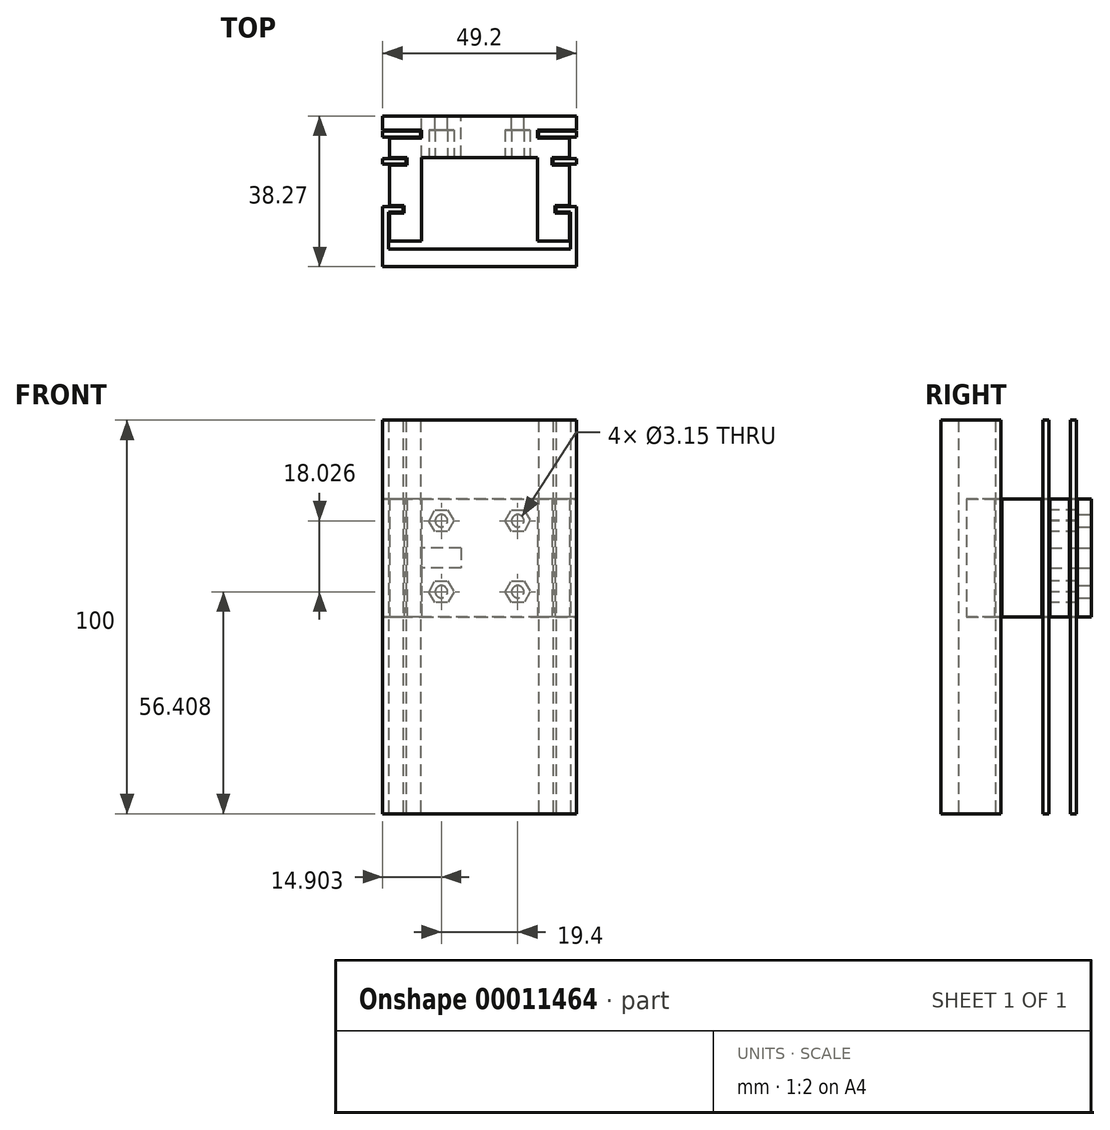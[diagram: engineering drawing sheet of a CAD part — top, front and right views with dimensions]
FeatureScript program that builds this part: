
annotation { "Feature Type Name" : "Feature", "Feature Type Description" : "" }
export const myFeature = defineFeature(function(context is Context, id is Id, definition is map)
    precondition{}
    {
        {
            var Q0;
            Q0=qCreatedBy(makeId("Top.planeOp"),FACE);
            var sketch = newSketch(context, id + "F0", { "sketchPlane" : qUnion([Q0])});
            skLineSegment(sketch, "E0.rect.bottom", {"start": v(-23.27, 11.03) * mm, "end": v(25.93, 11.03) * mm});
            skLineSegment(sketch, "E0.rect.top", {"start": v(-23.27, -23.37) * mm, "end": v(25.93, -23.37) * mm});
            skLineSegment(sketch, "E0.rect.left", {"start": v(-23.27, 11.03) * mm, "end": v(-23.27, -23.37) * mm});
            skLineSegment(sketch, "E0.rect.right", {"start": v(25.93, 11.03) * mm, "end": v(25.93, -23.37) * mm});
            skPoint(sketch, "E0.rect.middle", {"position": v(1.33, -6.17) * mm});
            skLineSegment(sketch, "E1", {"start": v(-13.62, 11.03) * mm, "end": v(-13.62, 9.53) * mm});
            skLineSegment(sketch, "E2", {"start": v(-13.62, 9.53) * mm, "end": v(-23.27, 9.53) * mm});
            skLineSegment(sketch, "E3", {"start": v(-23.27, 9.53) * mm, "end": v(-23.27, 4.13) * mm});
            skLineSegment(sketch, "E4", {"start": v(-23.27, 4.13) * mm, "end": v(-17.37, 4.13) * mm});
            skLineSegment(sketch, "E5", {"start": v(-17.37, 4.13) * mm, "end": v(-17.37, 2.63) * mm});
            skLineSegment(sketch, "E6", {"start": v(-17.37, 2.63) * mm, "end": v(-23.27, 2.63) * mm});
            skLineSegment(sketch, "E7", {"start": v(-23.27, 2.63) * mm, "end": v(-23.27, -8.04) * mm});
            skLineSegment(sketch, "E8", {"start": v(-23.27, -8.04) * mm, "end": v(-18.07, -8.04) * mm});
            skLineSegment(sketch, "E9", {"start": v(-18.07, -8.04) * mm, "end": v(-18.07, -9.54) * mm});
            skLineSegment(sketch, "E10", {"start": v(-18.07, -9.54) * mm, "end": v(-23.27, -9.54) * mm});
            skLineSegment(sketch, "E11", {"start": v(16.28, 11.03) * mm, "end": v(16.28, 9.53) * mm});
            skLineSegment(sketch, "E12", {"start": v(16.28, 9.53) * mm, "end": v(25.93, 9.53) * mm});
            skLineSegment(sketch, "E13", {"start": v(25.93, 9.53) * mm, "end": v(25.93, 4.13) * mm});
            skLineSegment(sketch, "E14", {"start": v(25.93, 4.13) * mm, "end": v(20.03, 4.13) * mm});
            skLineSegment(sketch, "E15", {"start": v(20.03, 4.13) * mm, "end": v(20.03, 2.63) * mm});
            skLineSegment(sketch, "E16", {"start": v(20.03, 2.63) * mm, "end": v(25.93, 2.63) * mm});
            skLineSegment(sketch, "E17", {"start": v(25.93, 2.63) * mm, "end": v(25.93, -6.17) * mm});
            skLineSegment(sketch, "E18", {"start": v(25.93, -8.04) * mm, "end": v(20.73, -8.04) * mm});
            skLineSegment(sketch, "E19", {"start": v(20.73, -8.04) * mm, "end": v(20.73, -9.54) * mm});
            skLineSegment(sketch, "E20", {"start": v(20.73, -9.54) * mm, "end": v(25.93, -9.54) * mm});
            skLineSegment(sketch, "E21", {"start": v(-21.77, 11.03) * mm, "end": v(-21.77, -18.87) * mm});
            skLineSegment(sketch, "E22", {"start": v(-21.77, -18.87) * mm, "end": v(24.43, -18.87) * mm});
            skLineSegment(sketch, "E23", {"start": v(24.43, -18.87) * mm, "end": v(24.43, 9.53) * mm});
            skLineSegment(sketch, "E24", {"start": v(-21.77, 11.28) * mm, "end": v(-21.77, 15.19) * mm});
            skLineSegment(sketch, "E25", {"start": v(-21.77, 15.19) * mm, "end": v(24.43, 15.19) * mm});
            skLineSegment(sketch, "E26", {"start": v(24.43, 15.19) * mm, "end": v(24.43, 11.28) * mm});
            skLineSegment(sketch, "E27", {"start": v(24.43, 11.28) * mm, "end": v(16.03, 11.28) * mm});
            skLineSegment(sketch, "E28", {"start": v(16.03, 11.28) * mm, "end": v(16.03, 9.28) * mm});
            skLineSegment(sketch, "E29", {"start": v(16.03, 9.28) * mm, "end": v(24.18, 9.28) * mm});
            skLineSegment(sketch, "E30", {"start": v(24.18, 9.28) * mm, "end": v(24.18, 4.38) * mm});
            skLineSegment(sketch, "E31", {"start": v(24.18, 4.38) * mm, "end": v(19.78, 4.38) * mm});
            skLineSegment(sketch, "E32", {"start": v(19.78, 4.38) * mm, "end": v(19.78, 2.38) * mm});
            skLineSegment(sketch, "E33", {"start": v(19.78, 2.38) * mm, "end": v(24.18, 2.38) * mm});
            skLineSegment(sketch, "E34", {"start": v(24.18, 2.38) * mm, "end": v(24.18, -7.79) * mm});
            skLineSegment(sketch, "E35", {"start": v(24.18, -7.79) * mm, "end": v(20.48, -7.79) * mm});
            skLineSegment(sketch, "E36", {"start": v(20.48, -7.79) * mm, "end": v(20.48, -9.79) * mm});
            skLineSegment(sketch, "E37", {"start": v(20.48, -9.79) * mm, "end": v(24.18, -9.79) * mm});
            skLineSegment(sketch, "E38", {"start": v(24.18, -9.79) * mm, "end": v(24.18, -13.4) * mm});
            skLineSegment(sketch, "E39", {"start": v(24.18, -13.4) * mm, "end": v(-21.52, -13.4) * mm});
            skLineSegment(sketch, "E40", {"start": v(-21.52, -13.4) * mm, "end": v(-21.52, -9.79) * mm});
            skLineSegment(sketch, "E41", {"start": v(-21.52, -9.79) * mm, "end": v(-17.82, -9.79) * mm});
            skLineSegment(sketch, "E42", {"start": v(-17.82, -9.79) * mm, "end": v(-17.82, -7.79) * mm});
            skLineSegment(sketch, "E43", {"start": v(-17.82, -7.79) * mm, "end": v(-21.52, -7.79) * mm});
            skLineSegment(sketch, "E44", {"start": v(-21.52, -7.79) * mm, "end": v(-21.52, 2.38) * mm});
            skLineSegment(sketch, "E45", {"start": v(-21.52, 2.38) * mm, "end": v(-17.12, 2.38) * mm});
            skLineSegment(sketch, "E46", {"start": v(-17.12, 2.38) * mm, "end": v(-17.12, 4.38) * mm});
            skLineSegment(sketch, "E47", {"start": v(-17.12, 4.38) * mm, "end": v(-21.52, 4.38) * mm});
            skLineSegment(sketch, "E48", {"start": v(-21.52, 4.38) * mm, "end": v(-21.52, 9.28) * mm});
            skLineSegment(sketch, "E49", {"start": v(-21.52, 9.28) * mm, "end": v(-13.37, 9.28) * mm});
            skLineSegment(sketch, "E50", {"start": v(-13.37, 9.28) * mm, "end": v(-13.37, 11.28) * mm});
            skLineSegment(sketch, "E51", {"start": v(-13.37, 11.28) * mm, "end": v(-21.77, 11.28) * mm});
            skLineSegment(sketch, "E52", {"start": v(-21.52, -11.6) * mm, "end": v(-21.77, -11.6) * mm});
            skLineSegment(sketch, "E53", {"start": v(-21.52, -2.7) * mm, "end": v(-21.77, -2.7) * mm});
            skLineSegment(sketch, "E54", {"start": v(-17.82, -8.43) * mm, "end": v(-18.07, -8.43) * mm});
            skLineSegment(sketch, "E55", {"start": v(-17.12, 3.38) * mm, "end": v(-17.37, 3.38) * mm});
            skLineSegment(sketch, "E56", {"start": v(-19.67, -9.79) * mm, "end": v(-19.67, -9.54) * mm});
            skLineSegment(sketch, "E57", {"start": v(-19.3, -8.04) * mm, "end": v(-19.3, -7.79) * mm});
            skLineSegment(sketch, "E58", {"start": v(-18.52, 2.38) * mm, "end": v(-18.52, 2.63) * mm});
            skLineSegment(sketch, "E59", {"start": v(-18.54, 4.13) * mm, "end": v(-18.54, 4.38) * mm});
            skLineSegment(sketch, "E60", {"start": v(-18.03, 9.28) * mm, "end": v(-18.03, 9.53) * mm});
            skLineSegment(sketch, "E61", {"start": v(-18.25, 11.03) * mm, "end": v(-18.25, 11.28) * mm});
            skLineSegment(sketch, "E62", {"start": v(16.03, 10.24) * mm, "end": v(16.28, 10.24) * mm});
            skLineSegment(sketch, "E63", {"start": v(24.18, 7.36) * mm, "end": v(24.43, 7.36) * mm});
            skLineSegment(sketch, "E64", {"start": v(19.78, 3.38) * mm, "end": v(20.03, 3.38) * mm});
            skLineSegment(sketch, "E65", {"start": v(24.18, -1.9) * mm, "end": v(24.43, -1.9) * mm});
            skLineSegment(sketch, "E66", {"start": v(20.48, -8.79) * mm, "end": v(20.73, -8.79) * mm});
            skLineSegment(sketch, "E67", {"start": v(24.18, -11.6) * mm, "end": v(24.43, -11.6) * mm});
            skLineSegment(sketch, "E68", {"start": v(-13.62, 10.28) * mm, "end": v(-13.37, 10.28) * mm});
            skSolve(sketch);
        }
        {
            var Q0;
            {var subQ13=sQuery(id+"F0.wireOp",EDGE,"E0.rect.top");Q0=makeQuery(id+"F0.imprint","IMPRINT",FACE,{"disambiguationData":[TD([[makeQuery(id+"F0.imprint","IMPRINT",EDGE,{"derivedFrom":subQ13}),1.0]])]});}
            var Q1;
            {var subQ3=sQuery(id+"F0.wireOp",EDGE,"E8");var subQ10=makeQuery(id+"F0.imprint","INTERSECT",VERTEX,{"derivedFrom":[subQ3,sQuery(id+"F0.wireOp",EDGE,"E57")]});Q1=makeQuery(id+"F0.imprint","IMPRINT",FACE,{"disambiguationData":[TD([[makeQuery(id+"F0.imprint","IMPRINT",EDGE,{"disambiguationData":[TD([[subQ10,1.0]])],"derivedFrom":subQ3}),-1.0]])]});}
            var Q2;
            {var subQ1=sQuery(id+"F0.wireOp",EDGE,"E10");var subQ5=sQuery(id+"F0.wireOp",EDGE,"E0.rect.left");var subQ6=makeQuery(id+"F0.imprint","INTERSECT",VERTEX,{"derivedFrom":[subQ5,subQ1]});Q2=makeQuery(id+"F0.imprint","IMPRINT",FACE,{"disambiguationData":[TD([[makeQuery(id+"F0.imprint","IMPRINT",EDGE,{"disambiguationData":[TD([[subQ6,1.0]])],"derivedFrom":subQ1}),-1.0]])]});}
            var Q3;
            {var subQ7=sQuery(id+"F0.wireOp",EDGE,"E7");Q3=makeQuery(id+"F0.imprint","IMPRINT",FACE,{"disambiguationData":[TD([[makeQuery(id+"F0.imprint","IMPRINT",EDGE,{"derivedFrom":subQ7}),1.0]])]});}
            var Q4;
            {var subQ0=sQuery(id+"F0.wireOp",EDGE,"E21");var subQ3=sQuery(id+"F0.wireOp",EDGE,"E4");var subQ4=makeQuery(id+"F0.imprint","INTERSECT",VERTEX,{"derivedFrom":[subQ3,subQ0]});Q4=makeQuery(id+"F0.imprint","IMPRINT",FACE,{"disambiguationData":[TD([[makeQuery(id+"F0.imprint","IMPRINT",EDGE,{"disambiguationData":[TD([[subQ4,-1.0]])],"derivedFrom":subQ0}),-1.0]])]});}
            var Q5;
            {var subQ3=sQuery(id+"F0.wireOp",EDGE,"E4");var subQ10=makeQuery(id+"F0.imprint","INTERSECT",VERTEX,{"derivedFrom":[subQ3,sQuery(id+"F0.wireOp",EDGE,"E59")]});Q5=makeQuery(id+"F0.imprint","IMPRINT",FACE,{"disambiguationData":[TD([[makeQuery(id+"F0.imprint","IMPRINT",EDGE,{"disambiguationData":[TD([[subQ10,1.0]])],"derivedFrom":subQ3}),-1.0]])]});}
            var Q6;
            {var subQ6=sQuery(id+"F0.wireOp",EDGE,"E3");Q6=makeQuery(id+"F0.imprint","IMPRINT",FACE,{"disambiguationData":[TD([[makeQuery(id+"F0.imprint","IMPRINT",EDGE,{"derivedFrom":subQ6}),1.0]])]});}
            var Q7;
            {var subQ3=sQuery(id+"F0.wireOp",EDGE,"E0.rect.bottom");var subQ5=sQuery(id+"F0.wireOp",EDGE,"E0.rect.left");var subQ7=makeQuery(id+"F0.imprint","INTERSECT",VERTEX,{"derivedFrom":[subQ3,subQ5]});Q7=makeQuery(id+"F0.imprint","IMPRINT",FACE,{"disambiguationData":[TD([[makeQuery(id+"F0.imprint","IMPRINT",EDGE,{"disambiguationData":[TD([[subQ7,-1.0]])],"derivedFrom":subQ3}),-1.0]])]});}
            var Q8;
            {var subQ0=sQuery(id+"F0.wireOp",EDGE,"E21");var subQ3=sQuery(id+"F0.wireOp",EDGE,"E0.rect.bottom");var subQ4=makeQuery(id+"F0.imprint","INTERSECT",VERTEX,{"derivedFrom":[subQ3,subQ0]});Q8=makeQuery(id+"F0.imprint","IMPRINT",FACE,{"disambiguationData":[TD([[makeQuery(id+"F0.imprint","IMPRINT",EDGE,{"disambiguationData":[TD([[subQ4,-1.0]])],"derivedFrom":subQ3}),-1.0]])]});}
            var Q9;
            {var subQ3=sQuery(id+"F0.wireOp",EDGE,"E18");var subQ5=sQuery(id+"F0.wireOp",EDGE,"E0.rect.right");var subQ7=makeQuery(id+"F0.imprint","INTERSECT",VERTEX,{"derivedFrom":[subQ5,subQ3]});Q9=makeQuery(id+"F0.imprint","IMPRINT",FACE,{"disambiguationData":[TD([[makeQuery(id+"F0.imprint","IMPRINT",EDGE,{"disambiguationData":[TD([[subQ7,-1.0]])],"derivedFrom":subQ5}),-1.0]])]});}
            var Q10;
            {var subQ3=sQuery(id+"F0.wireOp",EDGE,"E18");var subQ5=sQuery(id+"F0.wireOp",EDGE,"E19");var subQ8=makeQuery(id+"F0.imprint","INTERSECT",VERTEX,{"derivedFrom":[subQ3,subQ5]});Q10=makeQuery(id+"F0.imprint","IMPRINT",FACE,{"disambiguationData":[TD([[makeQuery(id+"F0.imprint","IMPRINT",EDGE,{"disambiguationData":[TD([[subQ8,1.0]])],"derivedFrom":subQ3}),1.0]])]});}
            var Q11;
            {var subQ8=sQuery(id+"F0.wireOp",EDGE,"E17");Q11=makeQuery(id+"F0.imprint","IMPRINT",FACE,{"disambiguationData":[TD([[makeQuery(id+"F0.imprint","IMPRINT",EDGE,{"derivedFrom":subQ8}),-1.0]])]});}
            var Q12;
            {var subQ1=sQuery(id+"F0.wireOp",EDGE,"E23");var subQ5=sQuery(id+"F0.wireOp",EDGE,"E14");var subQ6=makeQuery(id+"F0.imprint","INTERSECT",VERTEX,{"derivedFrom":[subQ5,subQ1]});Q12=makeQuery(id+"F0.imprint","IMPRINT",FACE,{"disambiguationData":[TD([[makeQuery(id+"F0.imprint","IMPRINT",EDGE,{"disambiguationData":[TD([[subQ6,1.0]])],"derivedFrom":subQ1}),-1.0]])]});}
            var Q13;
            {var subQ3=sQuery(id+"F0.wireOp",EDGE,"E14");var subQ5=sQuery(id+"F0.wireOp",EDGE,"E15");var subQ8=makeQuery(id+"F0.imprint","INTERSECT",VERTEX,{"derivedFrom":[subQ3,subQ5]});Q13=makeQuery(id+"F0.imprint","IMPRINT",FACE,{"disambiguationData":[TD([[makeQuery(id+"F0.imprint","IMPRINT",EDGE,{"disambiguationData":[TD([[subQ8,1.0]])],"derivedFrom":subQ3}),1.0]])]});}
            var Q14;
            {var subQ7=sQuery(id+"F0.wireOp",EDGE,"E13");Q14=makeQuery(id+"F0.imprint","IMPRINT",FACE,{"disambiguationData":[TD([[makeQuery(id+"F0.imprint","IMPRINT",EDGE,{"derivedFrom":subQ7}),-1.0]])]});}
            var Q15;
            {var subQ2=sQuery(id+"F0.wireOp",EDGE,"E0.rect.right");var subQ7=sQuery(id+"F0.wireOp",EDGE,"E0.rect.bottom");var subQ9=makeQuery(id+"F0.imprint","INTERSECT",VERTEX,{"derivedFrom":[subQ7,subQ2]});Q15=makeQuery(id+"F0.imprint","IMPRINT",FACE,{"disambiguationData":[TD([[makeQuery(id+"F0.imprint","IMPRINT",EDGE,{"disambiguationData":[TD([[subQ9,1.0]])],"derivedFrom":subQ7}),-1.0]])]});}
            extrude(context, id + "F1", {"entities" : qUnion([Q0, Q1, Q2, Q3, Q4, Q5, Q6, Q7, Q8, Q9, Q10, Q11, Q12, Q13, Q14, Q15]), "endBound" : BoundingType.SYMMETRIC, "depth" : 100 * mm});
        }
        {
            var Q0;
            Q0=qCreatedBy(makeId("Top.planeOp"),FACE);
            var sketch = newSketch(context, id + "F2", { "sketchPlane" : qUnion([Q0])});
            skLineSegment(sketch, "E69", {"start": v(-23.27, 11.28) * mm, "end": v(-13.37, 11.28) * mm});
            skLineSegment(sketch, "E70", {"start": v(-13.37, 11.28) * mm, "end": v(-13.37, 9.28) * mm});
            skLineSegment(sketch, "E71", {"start": v(-13.37, 9.28) * mm, "end": v(-21.52, 9.28) * mm});
            skLineSegment(sketch, "E72", {"start": v(-21.52, 9.28) * mm, "end": v(-21.52, 4.38) * mm});
            skLineSegment(sketch, "E73", {"start": v(-21.52, 4.38) * mm, "end": v(-17.12, 4.38) * mm});
            skLineSegment(sketch, "E74", {"start": v(-17.12, 4.38) * mm, "end": v(-17.12, 2.38) * mm});
            skLineSegment(sketch, "E75", {"start": v(-17.12, 2.38) * mm, "end": v(-21.52, 2.38) * mm});
            skLineSegment(sketch, "E76", {"start": v(-21.52, 2.38) * mm, "end": v(-21.52, -7.79) * mm});
            skLineSegment(sketch, "E77", {"start": v(-21.52, -7.79) * mm, "end": v(-17.82, -7.79) * mm});
            skLineSegment(sketch, "E78", {"start": v(-17.82, -7.79) * mm, "end": v(-17.82, -9.79) * mm});
            skLineSegment(sketch, "E79", {"start": v(-21.52, -9.79) * mm, "end": v(-21.52, -16.85) * mm});
            skLineSegment(sketch, "E80", {"start": v(24.18, -16.9) * mm, "end": v(24.18, -9.79) * mm});
            skLineSegment(sketch, "E81", {"start": v(24.18, -9.79) * mm, "end": v(20.48, -9.79) * mm});
            skLineSegment(sketch, "E82", {"start": v(20.48, -9.79) * mm, "end": v(20.48, -7.79) * mm});
            skLineSegment(sketch, "E83", {"start": v(20.48, -7.79) * mm, "end": v(24.18, -7.79) * mm});
            skLineSegment(sketch, "E84", {"start": v(24.18, -7.79) * mm, "end": v(24.18, 2.38) * mm});
            skLineSegment(sketch, "E85", {"start": v(24.18, 2.38) * mm, "end": v(19.78, 2.38) * mm});
            skLineSegment(sketch, "E86", {"start": v(19.78, 2.38) * mm, "end": v(19.78, 4.38) * mm});
            skLineSegment(sketch, "E87", {"start": v(19.78, 4.38) * mm, "end": v(24.18, 4.38) * mm});
            skLineSegment(sketch, "E88", {"start": v(24.18, 4.38) * mm, "end": v(24.18, 9.28) * mm});
            skLineSegment(sketch, "E89", {"start": v(24.18, 9.28) * mm, "end": v(16.03, 9.28) * mm});
            skLineSegment(sketch, "E90", {"start": v(16.03, 9.28) * mm, "end": v(16.03, 11.28) * mm});
            skLineSegment(sketch, "E91", {"start": v(16.03, 11.28) * mm, "end": v(25.93, 11.28) * mm});
            skLineSegment(sketch, "E92", {"start": v(25.93, 11.28) * mm, "end": v(25.93, 14.9) * mm});
            skLineSegment(sketch, "E93", {"start": v(25.93, 14.9) * mm, "end": v(-23.27, 14.9) * mm});
            skLineSegment(sketch, "E94", {"start": v(-23.27, 14.9) * mm, "end": v(-23.27, 11.28) * mm});
            skLineSegment(sketch, "E95", {"start": v(-17.82, -9.79) * mm, "end": v(-21.52, -9.79) * mm});
            skLineSegment(sketch, "E96", {"start": v(-21.52, -16.85) * mm, "end": v(-13.37, -16.85) * mm});
            skLineSegment(sketch, "E97", {"start": v(-13.37, -16.85) * mm, "end": v(-13.37, 4.38) * mm});
            skLineSegment(sketch, "E98", {"start": v(-13.37, 4.38) * mm, "end": v(16.03, 4.38) * mm});
            skLineSegment(sketch, "E99", {"start": v(16.03, 4.38) * mm, "end": v(16.03, -16.9) * mm});
            skLineSegment(sketch, "E100", {"start": v(24.18, -16.9) * mm, "end": v(16.03, -16.9) * mm});
            skSolve(sketch);
        }
        {
            var Q0;
            Q0=makeQuery(id+"F2.imprint","IMPRINT",FACE,{"disambiguationData":[TD([[makeQuery(id+"F2.imprint","IMPRINT",EDGE,{"derivedFrom":sQuery(id+"F2.wireOp",EDGE,"E69")}),1.0]])]});
            extrude(context, id + "F3", {"entities" : qUnion([Q0]), "depth" : 30 * mm});
        }
        {
            var Q0;
            Q0=makeQuery(id+"F3.opExtrude","SWEPT_FACE",FACE,{"disambiguationData":[OSD([sQuery(id+"F2.wireOp",EDGE,"E93")])]});
            var sketch = newSketch(context, id + "F4", { "sketchPlane" : qUnion([Q0])});
            skLineSegment(sketch, "E101.bottom", {"start": v(3.37, 17.5) * mm, "end": v(13.37, 17.5) * mm});
            skLineSegment(sketch, "E101.top", {"start": v(3.37, 12.5) * mm, "end": v(13.37, 12.5) * mm});
            skLineSegment(sketch, "E101.left", {"start": v(3.37, 17.5) * mm, "end": v(3.37, 12.5) * mm});
            skLineSegment(sketch, "E101.right", {"start": v(13.37, 17.5) * mm, "end": v(13.37, 12.5) * mm});
            skCircle(sketch, "E102", {"center": v(8.37, 6.4) * mm, "radius": 1.32 * mm});
            skCircle(sketch, "E103", {"center": v(8.37, 24.43) * mm, "radius": 1.32 * mm});
            skCircle(sketch, "E104", {"center": v(-11.03, 24.43) * mm, "radius": 1.32 * mm});
            skCircle(sketch, "E105", {"center": v(-11.03, 6.4) * mm, "radius": 1.32 * mm});
            skSolve(sketch);
        }
        {
            var Q0;
            Q0=makeQuery(id+"F4.imprint","IMPRINT",FACE,{"disambiguationData":[TD([[makeQuery(id+"F4.imprint","IMPRINT",EDGE,{"derivedFrom":sQuery(id+"F4.wireOp",EDGE,"E101.bottom")}),-1.0]])]});
            extrude(context, id + "F5", {"entities" : qUnion([Q0]), "operationType" : NewBodyOperationType.REMOVE, "oppositeDirection" : true, "depth" : 25 * mm});
        }
        {
            var Q0;
            Q0=sQuery(id+"F4.wireOp",VERTEX,"E105.center");
            var Q1;
            Q1=sQuery(id+"F4.wireOp",VERTEX,"E102.center");
            var Q2;
            Q2=sQuery(id+"F4.wireOp",VERTEX,"E103.center");
            var Q3;
            Q3=sQuery(id+"F4.wireOp",VERTEX,"E104.center");
            var Q4;
            Q4=makeQuery(id+"F3.opExtrude","SWEPT_BODY",BODY,{"disambiguationData":[OSD([sQuery(id+"F2.wireOp",EDGE,"E69"),sQuery(id+"F2.wireOp",EDGE,"E70"),sQuery(id+"F2.wireOp",EDGE,"E71"),sQuery(id+"F2.wireOp",EDGE,"E72"),sQuery(id+"F2.wireOp",EDGE,"E73"),sQuery(id+"F2.wireOp",EDGE,"E74"),sQuery(id+"F2.wireOp",EDGE,"E75"),sQuery(id+"F2.wireOp",EDGE,"E76"),sQuery(id+"F2.wireOp",EDGE,"E77"),sQuery(id+"F2.wireOp",EDGE,"E78"),sQuery(id+"F2.wireOp",EDGE,"E79"),sQuery(id+"F2.wireOp",EDGE,"E80"),sQuery(id+"F2.wireOp",EDGE,"E81"),sQuery(id+"F2.wireOp",EDGE,"E82"),sQuery(id+"F2.wireOp",EDGE,"E83"),sQuery(id+"F2.wireOp",EDGE,"E84"),sQuery(id+"F2.wireOp",EDGE,"E85"),sQuery(id+"F2.wireOp",EDGE,"E86"),sQuery(id+"F2.wireOp",EDGE,"E87"),sQuery(id+"F2.wireOp",EDGE,"E88"),sQuery(id+"F2.wireOp",EDGE,"E89"),sQuery(id+"F2.wireOp",EDGE,"E90"),sQuery(id+"F2.wireOp",EDGE,"E91"),sQuery(id+"F2.wireOp",EDGE,"E92"),sQuery(id+"F2.wireOp",EDGE,"E93"),sQuery(id+"F2.wireOp",EDGE,"E94"),sQuery(id+"F2.wireOp",EDGE,"E95"),sQuery(id+"F2.wireOp",EDGE,"E96"),sQuery(id+"F2.wireOp",EDGE,"E97"),sQuery(id+"F2.wireOp",EDGE,"E98"),sQuery(id+"F2.wireOp",EDGE,"E99"),sQuery(id+"F2.wireOp",EDGE,"E100")])]});
            hole(context, id + "F6", {"style" : HoleStyle.SIMPLE, "holeDiameter" : 3.15 * mm, "endStyle" : HoleEndStyle.THROUGH, "locations" : qUnion([Q0, Q1, Q2, Q3]), "scope" : qUnion([Q4])});
        }
        {
            var Q0;
            Q0=makeQuery(id+"F3.opExtrude","SWEPT_FACE",FACE,{"disambiguationData":[OSD([sQuery(id+"F2.wireOp",EDGE,"E98")])]});
            var sketch = newSketch(context, id + "F7", { "sketchPlane" : qUnion([Q0])});
            skCircle(sketch, "E106.cCircle", {"center": v(-8.37, 24.43) * mm, "radius": 2.75 * mm, "construction": true});
            skLineSegment(sketch, "E106.0", {"start": v(-5.2, 24.45) * mm, "end": v(-6.76, 21.7) * mm});
            skLineSegment(sketch, "E106.1", {"start": v(-6.76, 21.7) * mm, "end": v(-9.94, 21.67) * mm});
            skLineSegment(sketch, "E106.2", {"start": v(-9.94, 21.67) * mm, "end": v(-11.54, 24.42) * mm});
            skLineSegment(sketch, "E106.3", {"start": v(-11.54, 24.42) * mm, "end": v(-9.97, 27.17) * mm});
            skLineSegment(sketch, "E106.4", {"start": v(-9.97, 27.17) * mm, "end": v(-6.8, 27.2) * mm});
            skLineSegment(sketch, "E106.5", {"start": v(-6.8, 27.2) * mm, "end": v(-5.2, 24.45) * mm});
            skPoint(sketch, "E106.0.midPoint", {"position": v(-5.98, 23.07) * mm});
            skCircle(sketch, "E107.cCircle", {"center": v(11.03, 24.43) * mm, "radius": 2.75 * mm, "construction": true});
            skLineSegment(sketch, "E107.0", {"start": v(7.86, 24.4) * mm, "end": v(9.42, 27.17) * mm});
            skLineSegment(sketch, "E107.1", {"start": v(9.42, 27.17) * mm, "end": v(12.6, 27.2) * mm});
            skLineSegment(sketch, "E107.2", {"start": v(12.6, 27.2) * mm, "end": v(14.2, 24.47) * mm});
            skLineSegment(sketch, "E107.3", {"start": v(14.2, 24.47) * mm, "end": v(12.65, 21.7) * mm});
            skLineSegment(sketch, "E107.4", {"start": v(12.65, 21.7) * mm, "end": v(9.47, 21.67) * mm});
            skLineSegment(sketch, "E107.5", {"start": v(9.47, 21.67) * mm, "end": v(7.86, 24.4) * mm});
            skPoint(sketch, "E107.0.midPoint", {"position": v(8.64, 25.78) * mm});
            skCircle(sketch, "E108.cCircle", {"center": v(11.03, 6.4) * mm, "radius": 2.75 * mm, "construction": true});
            skLineSegment(sketch, "E108.0", {"start": v(9.45, 9.16) * mm, "end": v(12.62, 9.16) * mm});
            skLineSegment(sketch, "E108.1", {"start": v(12.62, 9.16) * mm, "end": v(14.2, 6.4) * mm});
            skLineSegment(sketch, "E108.2", {"start": v(14.2, 6.4) * mm, "end": v(12.62, 3.66) * mm});
            skLineSegment(sketch, "E108.3", {"start": v(12.62, 3.66) * mm, "end": v(9.45, 3.66) * mm});
            skLineSegment(sketch, "E108.4", {"start": v(9.45, 3.66) * mm, "end": v(7.86, 6.4) * mm});
            skLineSegment(sketch, "E108.5", {"start": v(7.86, 6.4) * mm, "end": v(9.45, 9.16) * mm});
            skPoint(sketch, "E108.0.midPoint", {"position": v(11.03, 9.16) * mm});
            skCircle(sketch, "E109.cCircle", {"center": v(-8.37, 6.4) * mm, "radius": 2.75 * mm, "construction": true});
            skLineSegment(sketch, "E109.0", {"start": v(-9.95, 9.16) * mm, "end": v(-6.78, 9.16) * mm});
            skLineSegment(sketch, "E109.1", {"start": v(-6.78, 9.16) * mm, "end": v(-5.2, 6.4) * mm});
            skLineSegment(sketch, "E109.2", {"start": v(-5.2, 6.4) * mm, "end": v(-6.78, 3.66) * mm});
            skLineSegment(sketch, "E109.3", {"start": v(-6.78, 3.66) * mm, "end": v(-9.95, 3.66) * mm});
            skLineSegment(sketch, "E109.4", {"start": v(-9.95, 3.66) * mm, "end": v(-11.54, 6.4) * mm});
            skLineSegment(sketch, "E109.5", {"start": v(-11.54, 6.4) * mm, "end": v(-9.95, 9.16) * mm});
            skPoint(sketch, "E109.0.midPoint", {"position": v(-8.37, 9.16) * mm});
            skSolve(sketch);
        }
        {
            var Q0;
            Q0=makeQuery(id+"F7.imprint","IMPRINT",FACE,{"disambiguationData":[TD([[makeQuery(id+"F7.imprint","IMPRINT",EDGE,{"derivedFrom":sQuery(id+"F7.wireOp",EDGE,"E106.0")}),-1.0]])]});
            var Q1;
            Q1=makeQuery(id+"F7.imprint","IMPRINT",FACE,{"disambiguationData":[TD([[makeQuery(id+"F7.imprint","IMPRINT",EDGE,{"derivedFrom":sQuery(id+"F7.wireOp",EDGE,"E107.0")}),-1.0]])]});
            var Q2;
            Q2=makeQuery(id+"F7.imprint","IMPRINT",FACE,{"disambiguationData":[TD([[makeQuery(id+"F7.imprint","IMPRINT",EDGE,{"derivedFrom":sQuery(id+"F7.wireOp",EDGE,"E108.0")}),-1.0]])]});
            var Q3;
            Q3=makeQuery(id+"F7.imprint","IMPRINT",FACE,{"disambiguationData":[TD([[makeQuery(id+"F7.imprint","IMPRINT",EDGE,{"derivedFrom":sQuery(id+"F7.wireOp",EDGE,"E109.0")}),-1.0]])]});
            extrude(context, id + "F8", {"entities" : qUnion([Q0, Q1, Q2, Q3]), "operationType" : NewBodyOperationType.REMOVE, "oppositeDirection" : true, "depth" : 7 * mm});
        }
    });
